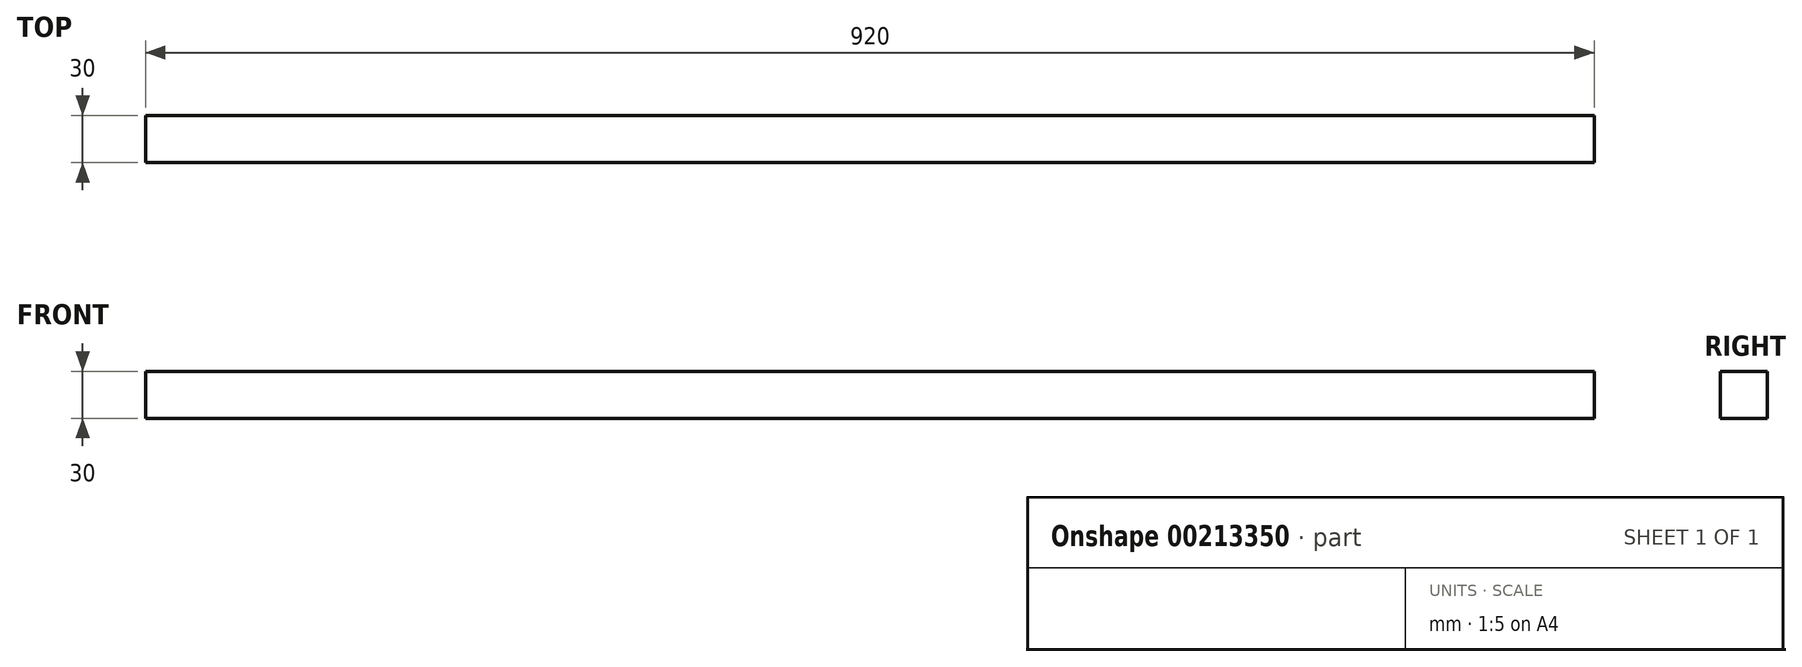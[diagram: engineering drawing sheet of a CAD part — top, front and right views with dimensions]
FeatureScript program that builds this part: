
annotation { "Feature Type Name" : "Feature", "Feature Type Description" : "" }
export const myFeature = defineFeature(function(context is Context, id is Id, definition is map)
    precondition{}
    {
        {
            var Q0;
            Q0=qCreatedBy(makeId("Top.planeOp"),FACE);
            var sketch = newSketch(context, id + "F0", { "sketchPlane" : qUnion([Q0])});
            skLineSegment(sketch, "E0.bottom", {"start": v(460, 15) * mm, "end": v(-460, 15) * mm});
            skLineSegment(sketch, "E0.top", {"start": v(460, -15) * mm, "end": v(-460, -15) * mm});
            skLineSegment(sketch, "E0.left", {"start": v(460, 15) * mm, "end": v(460, -15) * mm});
            skLineSegment(sketch, "E0.right", {"start": v(-460, 15) * mm, "end": v(-460, -15) * mm});
            skPoint(sketch, "E0.middle", {"position": v(0, 0) * mm});
            skSolve(sketch);
        }
        {
            var Q0;
            Q0=makeQuery(id+"F0.imprint","IMPRINT",FACE,{"disambiguationData":[TD([[makeQuery(id+"F0.imprint","IMPRINT",EDGE,{"derivedFrom":sQuery(id+"F0.wireOp",EDGE,"E0.bottom")}),1.0]])]});
            extrude(context, id + "F1", {"entities" : qUnion([Q0]), "depth" : 30 * mm});
        }
    });
